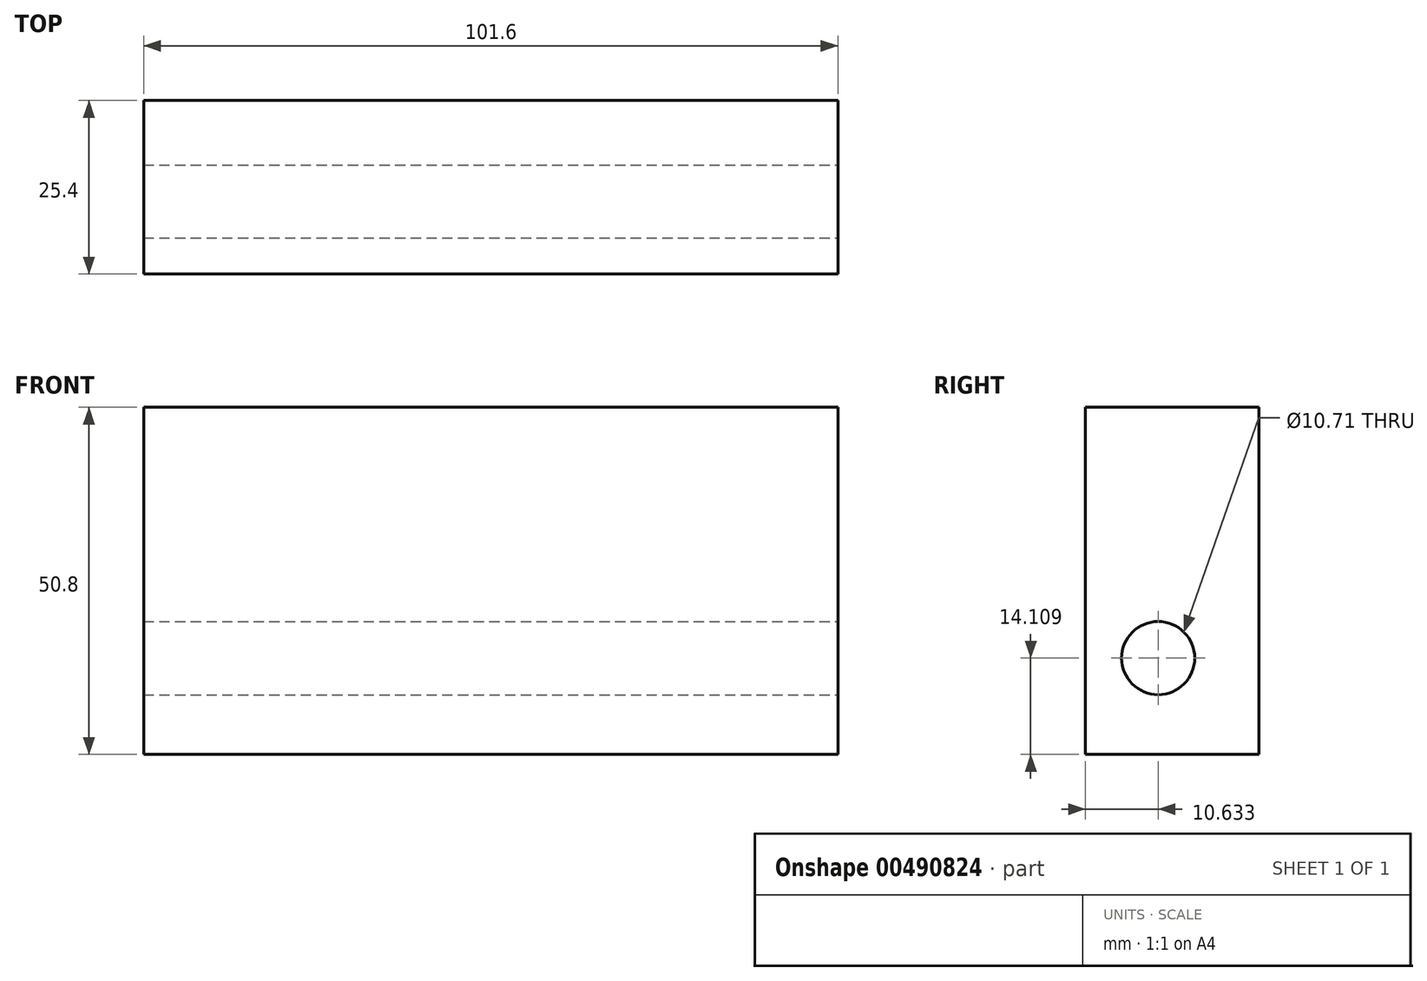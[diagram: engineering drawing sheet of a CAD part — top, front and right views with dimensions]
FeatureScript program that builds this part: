
annotation { "Feature Type Name" : "Feature", "Feature Type Description" : "" }
export const myFeature = defineFeature(function(context is Context, id is Id, definition is map)
    precondition{}
    {
        {
            var Q0;
            Q0=qCreatedBy(makeId("Front.planeOp"),FACE);
            var sketch = newSketch(context, id + "F0", { "sketchPlane" : qUnion([Q0])});
            skLineSegment(sketch, "E0.bottom", {"start": v(-50.8, -25.4) * mm, "end": v(50.8, -25.4) * mm});
            skLineSegment(sketch, "E0.top", {"start": v(-50.8, 25.4) * mm, "end": v(50.8, 25.4) * mm});
            skLineSegment(sketch, "E0.left", {"start": v(-50.8, -25.4) * mm, "end": v(-50.8, 25.4) * mm});
            skLineSegment(sketch, "E0.right", {"start": v(50.8, -25.4) * mm, "end": v(50.8, 25.4) * mm});
            skPoint(sketch, "E0.middle", {"position": v(0, 0) * mm});
            skSolve(sketch);
        }
        {
            var Q0;
            Q0 = qSketchRegion(id + "F0", true);
            extrude(context, id + "F1", {"entities" : qUnion([Q0]), "depth" : 25.4 * mm});
        }
        {
            var Q0;
            Q0=makeQuery(id+"F1.opExtrude","SWEPT_FACE",FACE,{"disambiguationData":[OSD([sQuery(id+"F0.wireOp",EDGE,"E0.right")])]});
            var sketch = newSketch(context, id + "F2", { "sketchPlane" : qUnion([Q0])});
            skCircle(sketch, "E1", {"center": v(-14.77, -11.3) * mm, "radius": 5.36 * mm});
            skSolve(sketch);
        }
        {
            var Q0;
            Q0 = qSketchRegion(id + "F2", true);
            extrude(context, id + "F3", {"entities" : qUnion([Q0]), "operationType" : NewBodyOperationType.REMOVE, "oppositeDirection" : true, "depth" : 127 * mm});
        }
    });
